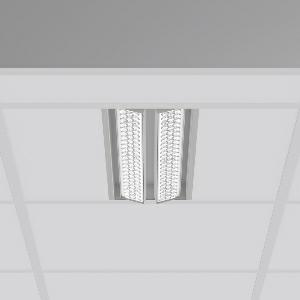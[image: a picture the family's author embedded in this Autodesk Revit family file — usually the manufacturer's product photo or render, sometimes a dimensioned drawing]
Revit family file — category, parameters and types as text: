
# Revit family: tx-move_901733_004_76_9dd4
name_source: partatom
category: Lighting Fixtures
units: mm (PartAtom-declared; Revit-internal decimal feet)

## family parameters
Cut with Voids When Loaded = No
Host = Face
Light Source = No
Part Type = Normal
Room Calculation Point = No
Round Connector Dimension = Use Diameter
Shared = No

## types (1)
- MultiLumen 1 (1 x LED Modul 830, 2800 lm, 3000)
    Apparent Load = 35 VA
    Approval mark = CE
    CIE Flux Codes = 77 96 99 100 100
    Color Rendering = 80
    Color Temperature = 3000
    Default Elevation = 1800 mm
    Description = Series: TX-MOVE
Einlege/Einbau-Flächenstrahler. Housing: sheet steel, powder-coated. 2xSwivel range: 90°. High-efficiency LED units with optimum light control thanks to clear plastic (PC) lens optics. Spezielle Mikrostrukturen reduzieren Gelbsaum. Symmetrical light distribution. Suitable for laying in grid ceiling module 600. Connected converter included in separate gearbox.Suitable for through-wiring.MultiLumen: Luminous flux adjustable in 3 steps. Accessories: Mounting frame for installation in suspended ceilings. Environmentally friendly and resource-saving due to replaceable and recyclable components. 
Colour: silver, matt (approx. RAL 9006)
Length: 597 mm
Width: 190 mm
Height: 39 mm
Cut-out length: 577.5 mm
Cut-out width: 174 mm
Recess height: 100 mm
Lamp: LED
Socket: without socket
Colour temperature: 3000K
Colour rendering index (CRI): 80
System power: 35 W
Rated luminous flux: 5600 lm
Luminous efficiency: 160 lm/W
System power 2: 47 W
Rated luminous flux 2: 7250 lm
Luminous efficiency 2: 154 lm/W
System power 3: 68 W
Rated luminous flux 3: 9850 lm
Luminous efficiency 3: 145 lm/W
Control gear: Dimmable EVG, DALI
Protection class: I
Type of protection: IP 20
    Height = 0 mm  [stored 0 ft]
    Lamp = 1 x LED Modul 830
    Lamp Light Flux = 2800 lm
    Lamp count = 1
    Length = 597 mm
    Lifetime = 50000 h
    Luminous efficacy = 160 lm/W
    Manufacturer = RZB
    ModVariant = No
    Model = 901733.004.76
    Mounting Place = Ceiling, Wall
    Mounting Type = Recessed
    Number of Poles = 1
    OnlyDefault = Yes
    Power Factor = 1
    Product Name = TX-MOVE
    Product group = Recessed projectors
    ProductGroupID = 401
    Protection Class = Protection class I
    Protection Degree = IP 20
    RLX_Detail_Level = 1
    RLX_Emergency_Light_Flux = 0 lm
    RLX_Emergency_Type = 0
    RLX_Emergency_Type_DB = No
    RlxData = <blob elided: 35653 chars, md5=7efa751f>
    Socket = socket
    Standby Power = 0 W
    System Light Flux = 5600 lm
    System Power = 35 W
    Type Comments = MultiLumen 1
    Type Image = 901733.004.jpg
    URL = http://relux.com
    VarID = multilumen_1
    Voltage = 230 V
    Voltage Range = 220-240 V
    Weight = 0.00 kg
    Width = 190 mm  [stored 0.62336 ft]

note: [stored X ft] marks values corroborated as IEEE doubles in the binary element streams (Revit-internal decimal feet)

## geometry (parser evidence)
native form markers: Blend x4, Sweep x12
no freeform markers — native parametric forms only
